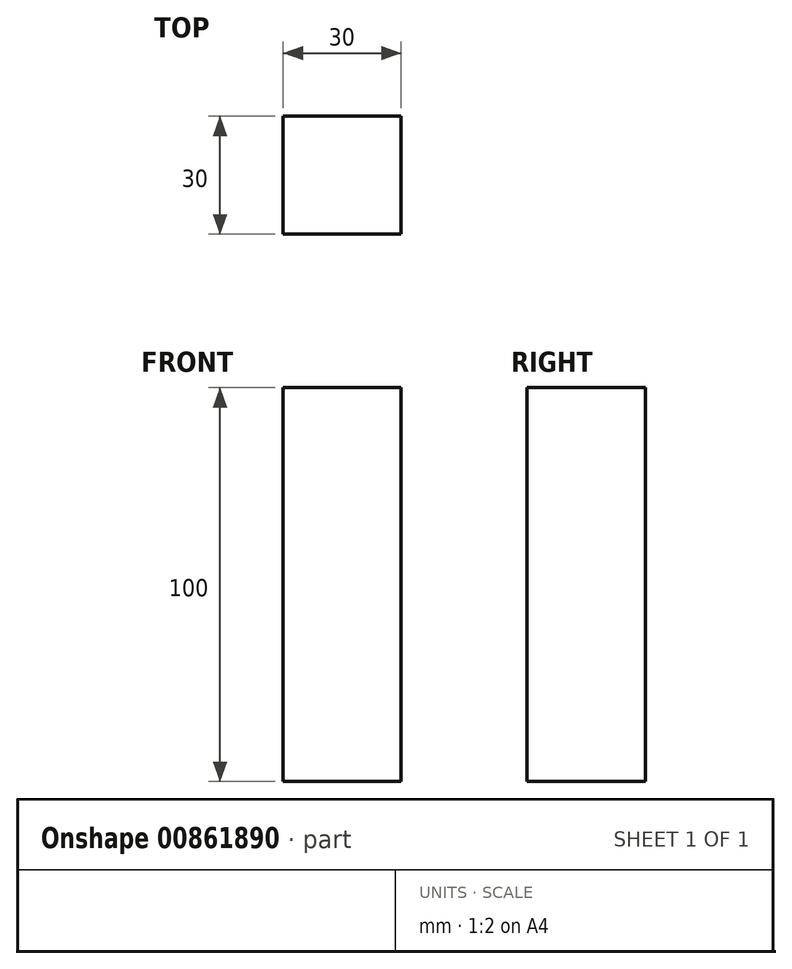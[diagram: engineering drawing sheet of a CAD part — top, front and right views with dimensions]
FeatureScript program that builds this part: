
annotation { "Feature Type Name" : "Feature", "Feature Type Description" : "" }
export const myFeature = defineFeature(function(context is Context, id is Id, definition is map)
    precondition{}
    {
        {
            var Q0;
            Q0=qCreatedBy(makeId("Top.planeOp"),FACE);
            var sketch = newSketch(context, id + "F0", { "sketchPlane" : qUnion([Q0])});
            skLineSegment(sketch, "E0.bottom", {"start": v(-15, -15) * mm, "end": v(15, -15) * mm});
            skLineSegment(sketch, "E0.top", {"start": v(-15, 15) * mm, "end": v(15, 15) * mm});
            skLineSegment(sketch, "E0.left", {"start": v(-15, -15) * mm, "end": v(-15, 15) * mm});
            skLineSegment(sketch, "E0.right", {"start": v(15, -15) * mm, "end": v(15, 15) * mm});
            skPoint(sketch, "E0.middle", {"position": v(0, 0) * mm});
            skSolve(sketch);
        }
        {
            var Q0;
            Q0 = qSketchRegion(id + "F0", true);
            extrude(context, id + "F1", {"entities" : qUnion([Q0]), "depth" : 100 * mm, "offsetDistance" : 25 * mm});
        }
    });
